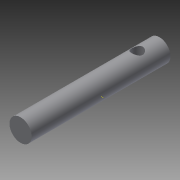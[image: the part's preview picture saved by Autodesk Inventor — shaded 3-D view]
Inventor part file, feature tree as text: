
AUTODESK INVENTOR PART (.ipt)
format: ipt  version: 2015 SP1 (Build 190203100, 203)  size: 79,360 bytes
history: native  units: mm
features: other x3, sketch x2, plane x1
ambient origin geometry x8: Origin, YZ Plane, XZ Plane, XY Plane, X Axis, Y Axis, Z Axis, Center Point
bodies: Solid1 (feature_tree)
feature tree (6):
  other  "Part3.ipt"
  other  "Solid2::Part3.ipt"
  other  "TaggingFeature1"
  sketch  "Sketch5"  dims[d0=10.0mm]
  sketch  "Sketch7"
  plane  "Work Plane1"
